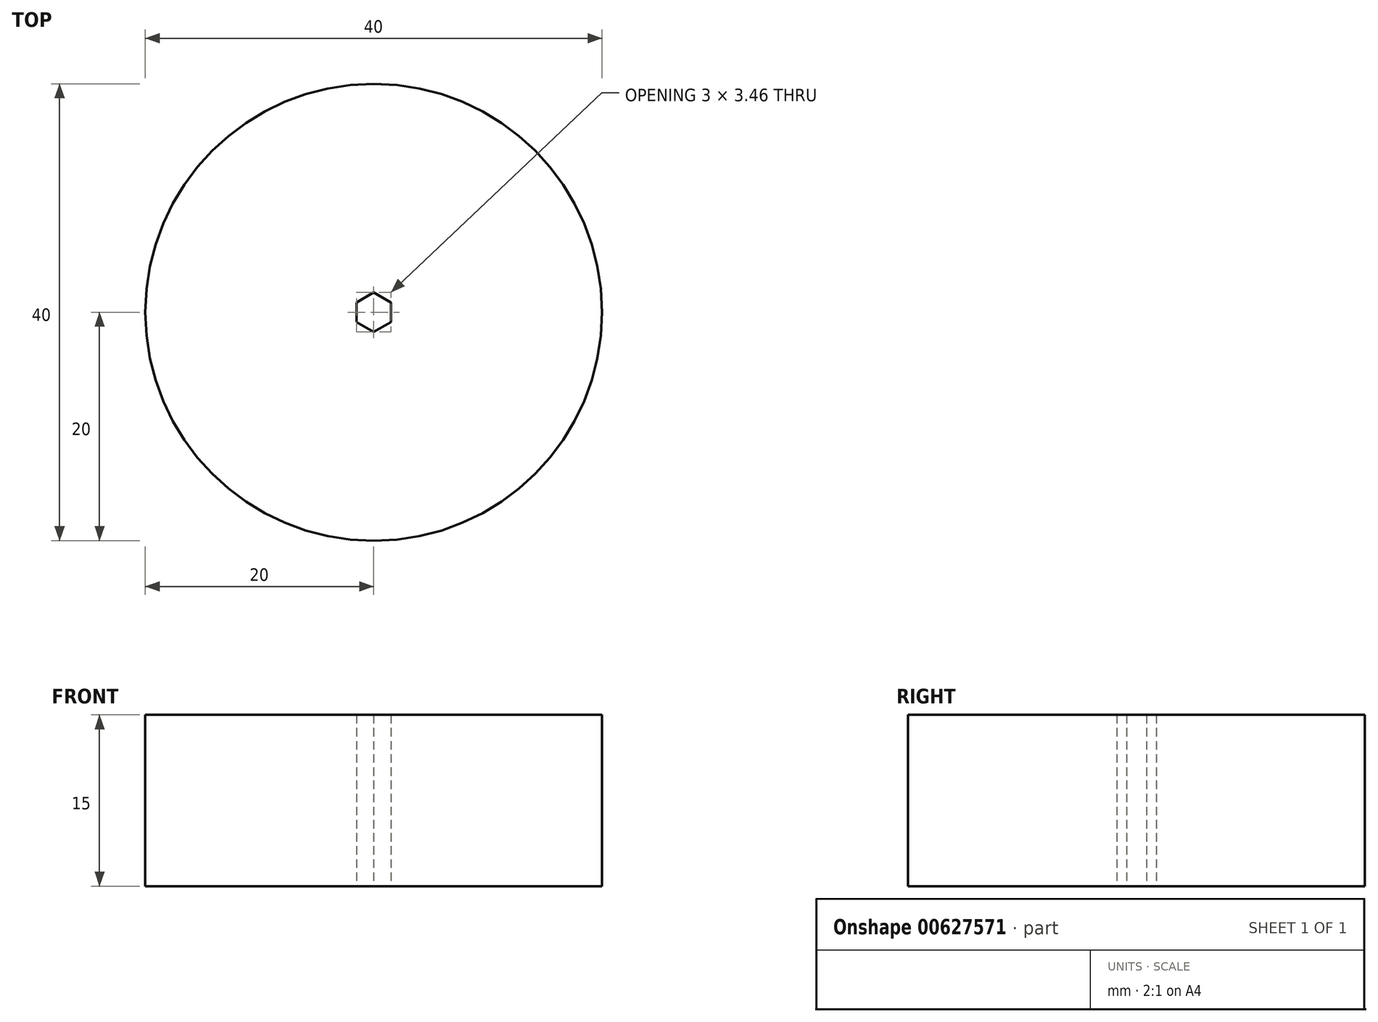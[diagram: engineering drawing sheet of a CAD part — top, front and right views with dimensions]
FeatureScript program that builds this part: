
annotation { "Feature Type Name" : "Feature", "Feature Type Description" : "" }
export const myFeature = defineFeature(function(context is Context, id is Id, definition is map)
    precondition{}
    {
        {
            var Q0;
            Q0=qCreatedBy(makeId("Top.planeOp"),FACE);
            var sketch = newSketch(context, id + "F0", { "sketchPlane" : qUnion([Q0])});
            skCircle(sketch, "E0", {"center": v(0, 0) * mm, "radius": 20 * mm});
            skCircle(sketch, "E1.cCircle", {"center": v(0, 0) * mm, "radius": 1.5 * mm, "construction": true});
            skLineSegment(sketch, "E1.0", {"start": v(1.5, 0.87) * mm, "end": v(1.5, -0.87) * mm});
            skLineSegment(sketch, "E1.1", {"start": v(1.5, -0.87) * mm, "end": v(0, -1.73) * mm});
            skLineSegment(sketch, "E1.2", {"start": v(0, -1.73) * mm, "end": v(-1.5, -0.87) * mm});
            skLineSegment(sketch, "E1.3", {"start": v(-1.5, -0.87) * mm, "end": v(-1.5, 0.87) * mm});
            skLineSegment(sketch, "E1.4", {"start": v(-1.5, 0.87) * mm, "end": v(0, 1.73) * mm});
            skLineSegment(sketch, "E1.5", {"start": v(0, 1.73) * mm, "end": v(1.5, 0.87) * mm});
            skPoint(sketch, "E1.0.midPoint", {"position": v(1.5, 0) * mm});
            skSolve(sketch);
        }
        {
            var Q0;
            Q0=makeQuery(id+"F0.imprint","IMPRINT",FACE,{"disambiguationData":[TD([[makeQuery(id+"F0.imprint","IMPRINT",EDGE,{"derivedFrom":sQuery(id+"F0.wireOp",EDGE,"E0")}),1.0]])]});
            extrude(context, id + "F1", {"entities" : qUnion([Q0]), "depth" : 15 * mm, "offsetDistance" : 25 * mm});
        }
    });
